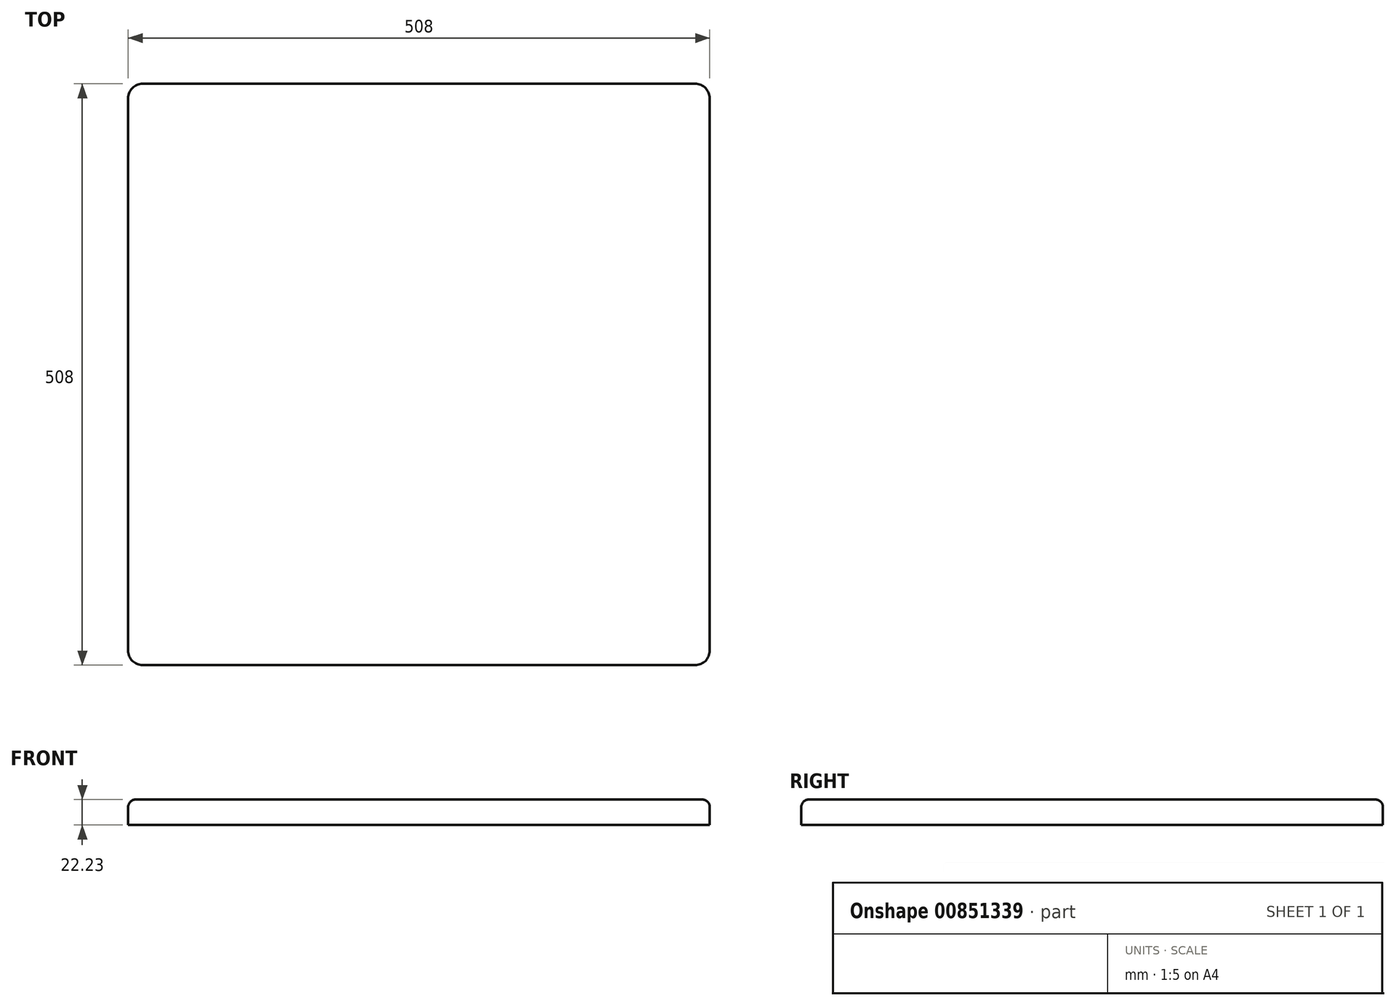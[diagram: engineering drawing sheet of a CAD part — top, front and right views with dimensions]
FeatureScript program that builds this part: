
annotation { "Feature Type Name" : "Feature", "Feature Type Description" : "" }
export const myFeature = defineFeature(function(context is Context, id is Id, definition is map)
    precondition{}
    {
        {
            var Q0;
            Q0=qCreatedBy(makeId("Top.planeOp"),FACE);
            var sketch = newSketch(context, id + "F0", { "sketchPlane" : qUnion([Q0])});
            skLineSegment(sketch, "E0.bottom", {"start": v(-254, 254) * mm, "end": v(254, 254) * mm});
            skLineSegment(sketch, "E0.top", {"start": v(-254, -254) * mm, "end": v(254, -254) * mm});
            skLineSegment(sketch, "E0.left", {"start": v(-254, 254) * mm, "end": v(-254, -254) * mm});
            skLineSegment(sketch, "E0.right", {"start": v(254, 254) * mm, "end": v(254, -254) * mm});
            skLineSegment(sketch, "E1", {"start": v(-254, 254) * mm, "end": v(254, -254) * mm, "construction": true});
            skSolve(sketch);
        }
        {
            var Q0;
            Q0 = qSketchRegion(id + "F0", true);
            extrude(context, id + "F1", {"entities" : qUnion([Q0]), "depth" : 22.22 * mm, "offsetDistance" : 25.4 * mm});
        }
        {
            var Q0;
            Q0=makeQuery(id+"F1.opExtrude","SWEPT_EDGE",EDGE,{"disambiguationData":[OSD([sQuery(id+"F0.wireOp",EDGE,"E0.top"),sQuery(id+"F0.wireOp",EDGE,"E0.left")])]});
            var Q1;
            Q1=makeQuery(id+"F1.opExtrude","SWEPT_EDGE",EDGE,{"disambiguationData":[OSD([sQuery(id+"F0.wireOp",EDGE,"E0.top"),sQuery(id+"F0.wireOp",EDGE,"E0.right")])]});
            var Q2;
            Q2=makeQuery(id+"F1.opExtrude","SWEPT_EDGE",EDGE,{"disambiguationData":[OSD([sQuery(id+"F0.wireOp",EDGE,"E0.bottom"),sQuery(id+"F0.wireOp",EDGE,"E0.right")])]});
            var Q3;
            Q3=makeQuery(id+"F1.opExtrude","SWEPT_EDGE",EDGE,{"disambiguationData":[OSD([sQuery(id+"F0.wireOp",EDGE,"E0.bottom"),sQuery(id+"F0.wireOp",EDGE,"E0.left")])]});
            fillet(context, id + "F2", {"entities" : qUnion([Q0, Q1, Q2, Q3]), "radius" : 12.7 * mm, "tangentPropagation" : true, "allowEdgeOverflow" : false});
        }
        {
            var Q0;
            Q0=makeQuery(id+"F1.opExtrude","CAP_EDGE",EDGE,{"disambiguationData":[OSD([sQuery(id+"F0.wireOp",EDGE,"E0.top")])],"isStart":false});
            fillet(context, id + "F3", {"entities" : qUnion([Q0]), "radius" : 6.35 * mm, "tangentPropagation" : true, "allowEdgeOverflow" : false});
        }
    });
